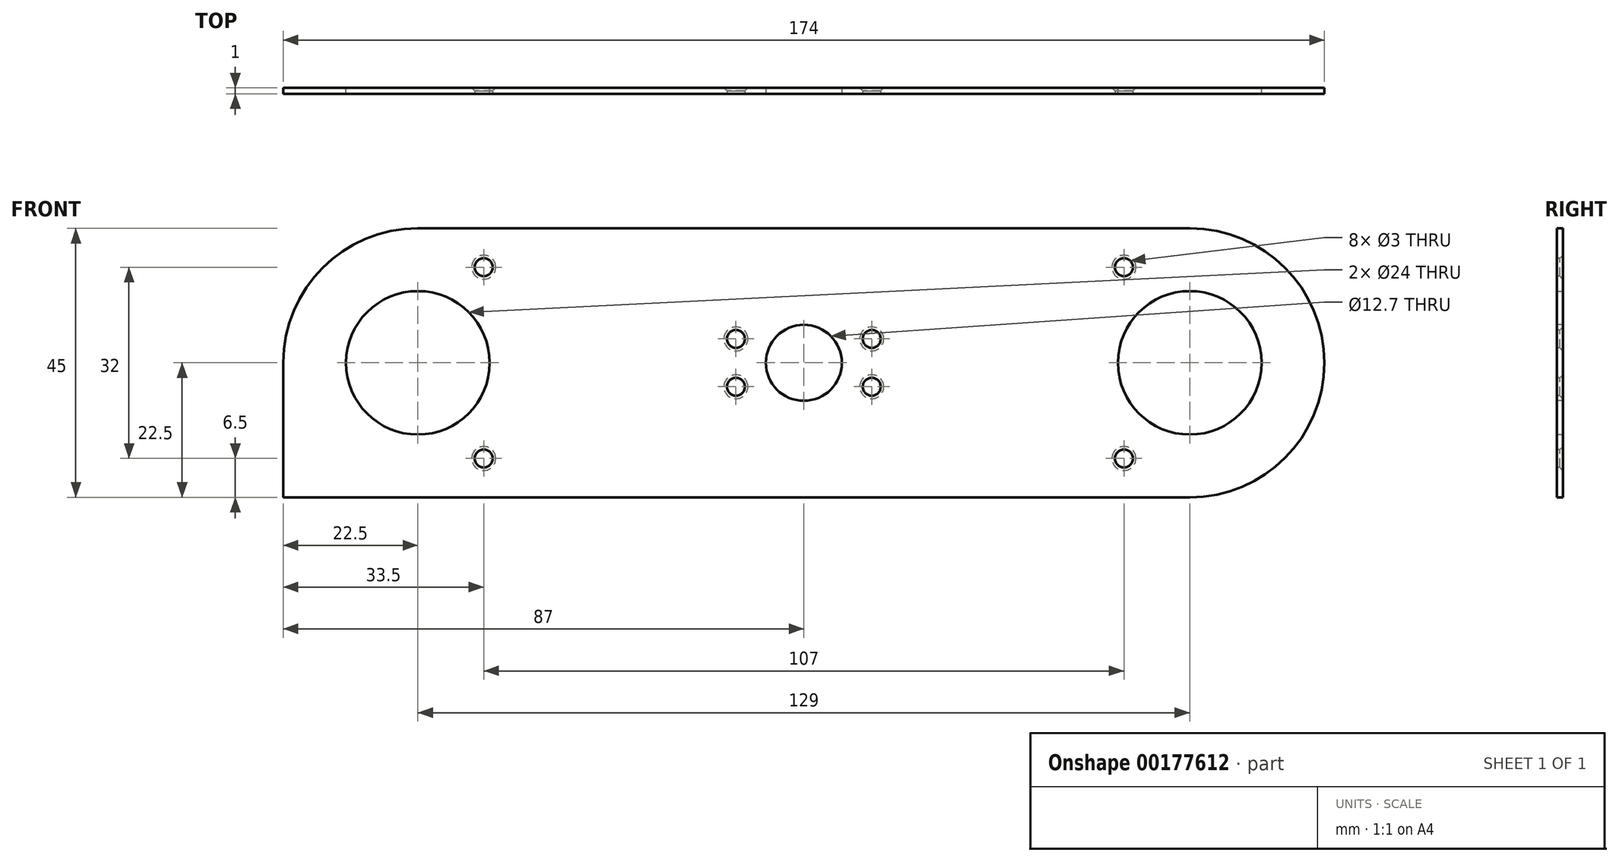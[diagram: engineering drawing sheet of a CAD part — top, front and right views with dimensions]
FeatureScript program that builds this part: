
annotation { "Feature Type Name" : "Feature", "Feature Type Description" : "" }
export const myFeature = defineFeature(function(context is Context, id is Id, definition is map)
    precondition{}
    {
        {
            var Q0;
            Q0=qCreatedBy(makeId("Front.planeOp"),FACE);
            var sketch = newSketch(context, id + "F0", { "sketchPlane" : qUnion([Q0])});
            skLineSegment(sketch, "E0.bottom", {"start": v(64.5, 22.5) * mm, "end": v(-64.5, 22.5) * mm});
            skLineSegment(sketch, "E0.top", {"start": v(64.5, -22.5) * mm, "end": v(-64.5, -22.5) * mm});
            skPoint(sketch, "E0.middle", {"position": v(0, 0) * mm});
            skCircle(sketch, "E1", {"center": v(64.5, 0) * mm, "radius": 12 * mm});
            skCircle(sketch, "E2", {"center": v(-64.5, 0) * mm, "radius": 12 * mm});
            skArc(sketch, "E3", {"start": v(-64.5, 22.5) * mm, "mid": v(-87, 0) * mm, "end": v(-64.5, -22.5) * mm});
            skArc(sketch, "E4", {"start": v(64.5, -22.5) * mm, "mid": v(87, 0) * mm, "end": v(64.5, 22.5) * mm});
            skPoint(sketch, "E5.orphan", {"position": v(-81.5, 22.5) * mm});
            skPoint(sketch, "E6.orphan", {"position": v(-81.5, -22.5) * mm});
            skPoint(sketch, "E7.orphan", {"position": v(81.5, 22.5) * mm});
            skPoint(sketch, "E8.orphan", {"position": v(81.5, -22.5) * mm});
            skSolve(sketch);
        }
        {
            var Q0;
            Q0 = qSketchRegion(id + "F0", true);
            extrude(context, id + "F1", {"entities" : qUnion([Q0]), "depth" : 1 * mm});
        }
        {
            var Q0;
            Q0=makeQuery(id+"F1.opExtrude","CAP_FACE",FACE,{"disambiguationData":[OSD([sQuery(id+"F0.wireOp",EDGE,"E0.bottom"),sQuery(id+"F0.wireOp",EDGE,"E0.top"),sQuery(id+"F0.wireOp",EDGE,"E1"),sQuery(id+"F0.wireOp",EDGE,"E2"),sQuery(id+"F0.wireOp",EDGE,"E3"),sQuery(id+"F0.wireOp",EDGE,"E4")])],"isStart":false});
            var sketch = newSketch(context, id + "F2", { "sketchPlane" : qUnion([Q0])});
            skLineSegment(sketch, "E9.top", {"start": v(-64.5, -22.5) * mm, "end": v(-87, -22.5) * mm});
            skLineSegment(sketch, "E9.right", {"start": v(-87, 0) * mm, "end": v(-87, -22.5) * mm});
            skPoint(sketch, "E9.left.start.orphan", {"position": v(-64.5, 0) * mm});
            skLineSegment(sketch, "E10", {"start": v(-87, 0) * mm, "end": v(-80.88, 0) * mm});
            skLineSegment(sketch, "E11", {"start": v(-80.88, 0) * mm, "end": v(-78.27, -9.46) * mm});
            skLineSegment(sketch, "E12", {"start": v(-78.27, -9.46) * mm, "end": v(-70.55, -14.76) * mm});
            skLineSegment(sketch, "E13", {"start": v(-70.55, -14.76) * mm, "end": v(-64.5, -17.43) * mm});
            skLineSegment(sketch, "E14", {"start": v(-64.5, -17.43) * mm, "end": v(-64.5, -22.5) * mm});
            skSolve(sketch);
        }
        {
            var Q0;
            Q0 = qSketchRegion(id + "F2", true);
            extrude(context, id + "F3", {"entities" : qUnion([Q0]), "operationType" : NewBodyOperationType.ADD, "oppositeDirection" : true, "depth" : 1 * mm});
        }
        {
            var Q0;
            Q0=makeQuery(id+"F3.boolean.opBoolean","MERGE",FACE,{"derivedFrom":[makeQuery(id+"F1.opExtrude","CAP_FACE",FACE,{"disambiguationData":[OSD([sQuery(id+"F0.wireOp",EDGE,"E0.bottom"),sQuery(id+"F0.wireOp",EDGE,"E0.top"),sQuery(id+"F0.wireOp",EDGE,"E1"),sQuery(id+"F0.wireOp",EDGE,"E2"),sQuery(id+"F0.wireOp",EDGE,"E3"),sQuery(id+"F0.wireOp",EDGE,"E4")])],"isStart":false}),makeQuery(id+"F3.opExtrude","CAP_FACE",FACE,{"disambiguationData":[OSD([sQuery(id+"F2.wireOp",EDGE,"E9.top"),sQuery(id+"F2.wireOp",EDGE,"E9.right"),sQuery(id+"F2.wireOp",EDGE,"E10"),sQuery(id+"F2.wireOp",EDGE,"E11"),sQuery(id+"F2.wireOp",EDGE,"E12"),sQuery(id+"F2.wireOp",EDGE,"E13"),sQuery(id+"F2.wireOp",EDGE,"E14")])],"isStart":true})]});
            var sketch = newSketch(context, id + "F4", { "sketchPlane" : qUnion([Q0])});
            skLineSegment(sketch, "E15.bottom", {"start": v(47, 22.5) * mm, "end": v(-47, 22.5) * mm, "construction": true});
            skLineSegment(sketch, "E15.top", {"start": v(47, -22.5) * mm, "end": v(-47, -22.5) * mm, "construction": true});
            skLineSegment(sketch, "E15.left", {"start": v(47, 22.5) * mm, "end": v(47, -22.5) * mm, "construction": true});
            skLineSegment(sketch, "E15.right", {"start": v(-47, 22.5) * mm, "end": v(-47, -22.5) * mm, "construction": true});
            skPoint(sketch, "E15.middle", {"position": v(0, 0) * mm});
            skLineSegment(sketch, "E16", {"start": v(-52.5, 0) * mm, "end": v(52.5, 0) * mm, "construction": true});
            skCircle(sketch, "E17", {"center": v(-53.5, 16) * mm, "radius": 1.5 * mm});
            skCircle(sketch, "E18", {"center": v(-53.5, -16) * mm, "radius": 1.5 * mm});
            skCircle(sketch, "E19", {"center": v(53.5, 16) * mm, "radius": 1.5 * mm});
            skCircle(sketch, "E20", {"center": v(53.5, -16) * mm, "radius": 1.5 * mm});
            skSolve(sketch);
        }
        {
            var Q0;
            Q0 = qSketchRegion(id + "F4", true);
            extrude(context, id + "F5", {"entities" : qUnion([Q0]), "operationType" : NewBodyOperationType.REMOVE, "oppositeDirection" : true, "depth" : 25 * mm});
        }
        {
            var Q0;
            Q0=makeQuery(id+"F5.boolean.opBoolean","INTERSECT",EDGE,{"derivedFrom":[makeQuery(id+"F3.boolean.opBoolean","MERGE",FACE,{"derivedFrom":[makeQuery(id+"F1.opExtrude","CAP_FACE",FACE,{"disambiguationData":[OSD([sQuery(id+"F0.wireOp",EDGE,"E0.bottom"),sQuery(id+"F0.wireOp",EDGE,"E0.top"),sQuery(id+"F0.wireOp",EDGE,"E1"),sQuery(id+"F0.wireOp",EDGE,"E2"),sQuery(id+"F0.wireOp",EDGE,"E3"),sQuery(id+"F0.wireOp",EDGE,"E4")])],"isStart":true}),makeQuery(id+"F3.opExtrude","CAP_FACE",FACE,{"disambiguationData":[OSD([sQuery(id+"F2.wireOp",EDGE,"E9.top"),sQuery(id+"F2.wireOp",EDGE,"E9.right"),sQuery(id+"F2.wireOp",EDGE,"E10"),sQuery(id+"F2.wireOp",EDGE,"E11"),sQuery(id+"F2.wireOp",EDGE,"E12"),sQuery(id+"F2.wireOp",EDGE,"E13"),sQuery(id+"F2.wireOp",EDGE,"E14")])],"isStart":false})]}),makeQuery(id+"F5.opExtrude","SWEPT_FACE",FACE,{"disambiguationData":[OSD([sQuery(id+"F4.wireOp",EDGE,"E17")])]})]});
            var Q1;
            Q1=makeQuery(id+"F5.boolean.opBoolean","INTERSECT",EDGE,{"derivedFrom":[makeQuery(id+"F3.boolean.opBoolean","MERGE",FACE,{"derivedFrom":[makeQuery(id+"F1.opExtrude","CAP_FACE",FACE,{"disambiguationData":[OSD([sQuery(id+"F0.wireOp",EDGE,"E0.bottom"),sQuery(id+"F0.wireOp",EDGE,"E0.top"),sQuery(id+"F0.wireOp",EDGE,"E1"),sQuery(id+"F0.wireOp",EDGE,"E2"),sQuery(id+"F0.wireOp",EDGE,"E3"),sQuery(id+"F0.wireOp",EDGE,"E4")])],"isStart":true}),makeQuery(id+"F3.opExtrude","CAP_FACE",FACE,{"disambiguationData":[OSD([sQuery(id+"F2.wireOp",EDGE,"E9.top"),sQuery(id+"F2.wireOp",EDGE,"E9.right"),sQuery(id+"F2.wireOp",EDGE,"E10"),sQuery(id+"F2.wireOp",EDGE,"E11"),sQuery(id+"F2.wireOp",EDGE,"E12"),sQuery(id+"F2.wireOp",EDGE,"E13"),sQuery(id+"F2.wireOp",EDGE,"E14")])],"isStart":false})]}),makeQuery(id+"F5.opExtrude","SWEPT_FACE",FACE,{"disambiguationData":[OSD([sQuery(id+"F4.wireOp",EDGE,"E18")])]})]});
            var Q2;
            Q2=makeQuery(id+"F5.boolean.opBoolean","INTERSECT",EDGE,{"derivedFrom":[makeQuery(id+"F3.boolean.opBoolean","MERGE",FACE,{"derivedFrom":[makeQuery(id+"F1.opExtrude","CAP_FACE",FACE,{"disambiguationData":[OSD([sQuery(id+"F0.wireOp",EDGE,"E0.bottom"),sQuery(id+"F0.wireOp",EDGE,"E0.top"),sQuery(id+"F0.wireOp",EDGE,"E1"),sQuery(id+"F0.wireOp",EDGE,"E2"),sQuery(id+"F0.wireOp",EDGE,"E3"),sQuery(id+"F0.wireOp",EDGE,"E4")])],"isStart":true}),makeQuery(id+"F3.opExtrude","CAP_FACE",FACE,{"disambiguationData":[OSD([sQuery(id+"F2.wireOp",EDGE,"E9.top"),sQuery(id+"F2.wireOp",EDGE,"E9.right"),sQuery(id+"F2.wireOp",EDGE,"E10"),sQuery(id+"F2.wireOp",EDGE,"E11"),sQuery(id+"F2.wireOp",EDGE,"E12"),sQuery(id+"F2.wireOp",EDGE,"E13"),sQuery(id+"F2.wireOp",EDGE,"E14")])],"isStart":false})]}),makeQuery(id+"F5.opExtrude","SWEPT_FACE",FACE,{"disambiguationData":[OSD([sQuery(id+"F4.wireOp",EDGE,"E19")])]})]});
            var Q3;
            Q3=makeQuery(id+"F5.boolean.opBoolean","INTERSECT",EDGE,{"derivedFrom":[makeQuery(id+"F3.boolean.opBoolean","MERGE",FACE,{"derivedFrom":[makeQuery(id+"F1.opExtrude","CAP_FACE",FACE,{"disambiguationData":[OSD([sQuery(id+"F0.wireOp",EDGE,"E0.bottom"),sQuery(id+"F0.wireOp",EDGE,"E0.top"),sQuery(id+"F0.wireOp",EDGE,"E1"),sQuery(id+"F0.wireOp",EDGE,"E2"),sQuery(id+"F0.wireOp",EDGE,"E3"),sQuery(id+"F0.wireOp",EDGE,"E4")])],"isStart":true}),makeQuery(id+"F3.opExtrude","CAP_FACE",FACE,{"disambiguationData":[OSD([sQuery(id+"F2.wireOp",EDGE,"E9.top"),sQuery(id+"F2.wireOp",EDGE,"E9.right"),sQuery(id+"F2.wireOp",EDGE,"E10"),sQuery(id+"F2.wireOp",EDGE,"E11"),sQuery(id+"F2.wireOp",EDGE,"E12"),sQuery(id+"F2.wireOp",EDGE,"E13"),sQuery(id+"F2.wireOp",EDGE,"E14")])],"isStart":false})]}),makeQuery(id+"F5.opExtrude","SWEPT_FACE",FACE,{"disambiguationData":[OSD([sQuery(id+"F4.wireOp",EDGE,"E20")])]})]});
            chamfer(context, id + "F6", {"entities" : qUnion([Q0, Q1, Q2, Q3]), "width" : .5 * mm, "tangentPropagation" : true});
        }
        {
            var Q0;
            Q0=makeQuery(id+"F3.boolean.opBoolean","MERGE",FACE,{"derivedFrom":[makeQuery(id+"F1.opExtrude","CAP_FACE",FACE,{"disambiguationData":[OSD([sQuery(id+"F0.wireOp",EDGE,"E0.bottom"),sQuery(id+"F0.wireOp",EDGE,"E0.top"),sQuery(id+"F0.wireOp",EDGE,"E1"),sQuery(id+"F0.wireOp",EDGE,"E2"),sQuery(id+"F0.wireOp",EDGE,"E3"),sQuery(id+"F0.wireOp",EDGE,"E4")])],"isStart":false}),makeQuery(id+"F3.opExtrude","CAP_FACE",FACE,{"disambiguationData":[OSD([sQuery(id+"F2.wireOp",EDGE,"E9.top"),sQuery(id+"F2.wireOp",EDGE,"E9.right"),sQuery(id+"F2.wireOp",EDGE,"E10"),sQuery(id+"F2.wireOp",EDGE,"E11"),sQuery(id+"F2.wireOp",EDGE,"E12"),sQuery(id+"F2.wireOp",EDGE,"E13"),sQuery(id+"F2.wireOp",EDGE,"E14")])],"isStart":true})]});
            var sketch = newSketch(context, id + "F7", { "sketchPlane" : qUnion([Q0])});
            skCircle(sketch, "E21", {"center": v(0, 0) * mm, "radius": 6.35 * mm});
            skSolve(sketch);
        }
        {
            var Q0;
            Q0 = qSketchRegion(id + "F7", true);
            extrude(context, id + "F8", {"entities" : qUnion([Q0]), "operationType" : NewBodyOperationType.REMOVE, "oppositeDirection" : true, "depth" : 25 * mm});
        }
        {
            var Q0;
            Q0=makeQuery(id+"F3.boolean.opBoolean","MERGE",FACE,{"derivedFrom":[makeQuery(id+"F1.opExtrude","CAP_FACE",FACE,{"disambiguationData":[OSD([sQuery(id+"F0.wireOp",EDGE,"E0.bottom"),sQuery(id+"F0.wireOp",EDGE,"E0.top"),sQuery(id+"F0.wireOp",EDGE,"E1"),sQuery(id+"F0.wireOp",EDGE,"E2"),sQuery(id+"F0.wireOp",EDGE,"E3"),sQuery(id+"F0.wireOp",EDGE,"E4")])],"isStart":false}),makeQuery(id+"F3.opExtrude","CAP_FACE",FACE,{"disambiguationData":[OSD([sQuery(id+"F2.wireOp",EDGE,"E9.top"),sQuery(id+"F2.wireOp",EDGE,"E9.right"),sQuery(id+"F2.wireOp",EDGE,"E10"),sQuery(id+"F2.wireOp",EDGE,"E11"),sQuery(id+"F2.wireOp",EDGE,"E12"),sQuery(id+"F2.wireOp",EDGE,"E13"),sQuery(id+"F2.wireOp",EDGE,"E14")])],"isStart":true})]});
            var sketch = newSketch(context, id + "F9", { "sketchPlane" : qUnion([Q0])});
            skPoint(sketch, "E22.middle", {"position": v(0, 0) * mm});
            skCircle(sketch, "E23", {"center": v(-11.35, 4) * mm, "radius": 1.5 * mm});
            skCircle(sketch, "E24", {"center": v(-11.35, -4) * mm, "radius": 1.5 * mm});
            skCircle(sketch, "E25", {"center": v(11.35, 4) * mm, "radius": 1.5 * mm});
            skCircle(sketch, "E26", {"center": v(11.35, -4) * mm, "radius": 1.5 * mm});
            skPoint(sketch, "E27.orphan", {"position": v(-11.35, 11.35) * mm});
            skPoint(sketch, "E28.orphan", {"position": v(11.35, 11.35) * mm});
            skPoint(sketch, "E22.top.start.orphan", {"position": v(11.35, -11.35) * mm});
            skPoint(sketch, "E29.orphan", {"position": v(-11.35, -11.35) * mm});
            skLineSegment(sketch, "E30", {"start": v(52.5, 0) * mm, "end": v(-52.5, 0) * mm, "construction": true});
            skLineSegment(sketch, "E31", {"start": v(-52.5, 0) * mm, "end": v(0, 0) * mm, "construction": true});
            skLineSegment(sketch, "E32", {"start": v(0, 22.5) * mm, "end": v(0, -22.5) * mm, "construction": true});
            skLineSegment(sketch, "E33.bottom", {"start": v(11.35, 11.35) * mm, "end": v(-11.35, 11.35) * mm, "construction": true});
            skLineSegment(sketch, "E33.top", {"start": v(11.35, -11.35) * mm, "end": v(-11.35, -11.35) * mm, "construction": true});
            skLineSegment(sketch, "E33.left", {"start": v(11.35, 11.35) * mm, "end": v(11.35, -11.35) * mm, "construction": true});
            skLineSegment(sketch, "E33.right", {"start": v(-11.35, 11.35) * mm, "end": v(-11.35, -11.35) * mm, "construction": true});
            skSolve(sketch);
        }
        {
            var Q0;
            Q0 = qSketchRegion(id + "F9", true);
            extrude(context, id + "F10", {"entities" : qUnion([Q0]), "operationType" : NewBodyOperationType.REMOVE, "oppositeDirection" : true, "depth" : 25 * mm});
        }
        {
            var Q0;
            Q0=makeQuery(id+"F10.boolean.opBoolean","INTERSECT",EDGE,{"derivedFrom":[makeQuery(id+"F3.boolean.opBoolean","MERGE",FACE,{"derivedFrom":[makeQuery(id+"F1.opExtrude","CAP_FACE",FACE,{"disambiguationData":[OSD([sQuery(id+"F0.wireOp",EDGE,"E0.bottom"),sQuery(id+"F0.wireOp",EDGE,"E0.top"),sQuery(id+"F0.wireOp",EDGE,"E1"),sQuery(id+"F0.wireOp",EDGE,"E2"),sQuery(id+"F0.wireOp",EDGE,"E3"),sQuery(id+"F0.wireOp",EDGE,"E4")])],"isStart":true}),makeQuery(id+"F3.opExtrude","CAP_FACE",FACE,{"disambiguationData":[OSD([sQuery(id+"F2.wireOp",EDGE,"E9.top"),sQuery(id+"F2.wireOp",EDGE,"E9.right"),sQuery(id+"F2.wireOp",EDGE,"E10"),sQuery(id+"F2.wireOp",EDGE,"E11"),sQuery(id+"F2.wireOp",EDGE,"E12"),sQuery(id+"F2.wireOp",EDGE,"E13"),sQuery(id+"F2.wireOp",EDGE,"E14")])],"isStart":false})]}),makeQuery(id+"F10.opExtrude","SWEPT_FACE",FACE,{"disambiguationData":[OSD([sQuery(id+"F9.wireOp",EDGE,"E23")])]})]});
            var Q1;
            Q1=makeQuery(id+"F10.boolean.opBoolean","INTERSECT",EDGE,{"derivedFrom":[makeQuery(id+"F3.boolean.opBoolean","MERGE",FACE,{"derivedFrom":[makeQuery(id+"F1.opExtrude","CAP_FACE",FACE,{"disambiguationData":[OSD([sQuery(id+"F0.wireOp",EDGE,"E0.bottom"),sQuery(id+"F0.wireOp",EDGE,"E0.top"),sQuery(id+"F0.wireOp",EDGE,"E1"),sQuery(id+"F0.wireOp",EDGE,"E2"),sQuery(id+"F0.wireOp",EDGE,"E3"),sQuery(id+"F0.wireOp",EDGE,"E4")])],"isStart":true}),makeQuery(id+"F3.opExtrude","CAP_FACE",FACE,{"disambiguationData":[OSD([sQuery(id+"F2.wireOp",EDGE,"E9.top"),sQuery(id+"F2.wireOp",EDGE,"E9.right"),sQuery(id+"F2.wireOp",EDGE,"E10"),sQuery(id+"F2.wireOp",EDGE,"E11"),sQuery(id+"F2.wireOp",EDGE,"E12"),sQuery(id+"F2.wireOp",EDGE,"E13"),sQuery(id+"F2.wireOp",EDGE,"E14")])],"isStart":false})]}),makeQuery(id+"F10.opExtrude","SWEPT_FACE",FACE,{"disambiguationData":[OSD([sQuery(id+"F9.wireOp",EDGE,"E24")])]})]});
            var Q2;
            Q2=makeQuery(id+"F10.boolean.opBoolean","INTERSECT",EDGE,{"derivedFrom":[makeQuery(id+"F3.boolean.opBoolean","MERGE",FACE,{"derivedFrom":[makeQuery(id+"F1.opExtrude","CAP_FACE",FACE,{"disambiguationData":[OSD([sQuery(id+"F0.wireOp",EDGE,"E0.bottom"),sQuery(id+"F0.wireOp",EDGE,"E0.top"),sQuery(id+"F0.wireOp",EDGE,"E1"),sQuery(id+"F0.wireOp",EDGE,"E2"),sQuery(id+"F0.wireOp",EDGE,"E3"),sQuery(id+"F0.wireOp",EDGE,"E4")])],"isStart":true}),makeQuery(id+"F3.opExtrude","CAP_FACE",FACE,{"disambiguationData":[OSD([sQuery(id+"F2.wireOp",EDGE,"E9.top"),sQuery(id+"F2.wireOp",EDGE,"E9.right"),sQuery(id+"F2.wireOp",EDGE,"E10"),sQuery(id+"F2.wireOp",EDGE,"E11"),sQuery(id+"F2.wireOp",EDGE,"E12"),sQuery(id+"F2.wireOp",EDGE,"E13"),sQuery(id+"F2.wireOp",EDGE,"E14")])],"isStart":false})]}),makeQuery(id+"F10.opExtrude","SWEPT_FACE",FACE,{"disambiguationData":[OSD([sQuery(id+"F9.wireOp",EDGE,"E26")])]})]});
            var Q3;
            Q3=makeQuery(id+"F10.boolean.opBoolean","INTERSECT",EDGE,{"derivedFrom":[makeQuery(id+"F3.boolean.opBoolean","MERGE",FACE,{"derivedFrom":[makeQuery(id+"F1.opExtrude","CAP_FACE",FACE,{"disambiguationData":[OSD([sQuery(id+"F0.wireOp",EDGE,"E0.bottom"),sQuery(id+"F0.wireOp",EDGE,"E0.top"),sQuery(id+"F0.wireOp",EDGE,"E1"),sQuery(id+"F0.wireOp",EDGE,"E2"),sQuery(id+"F0.wireOp",EDGE,"E3"),sQuery(id+"F0.wireOp",EDGE,"E4")])],"isStart":true}),makeQuery(id+"F3.opExtrude","CAP_FACE",FACE,{"disambiguationData":[OSD([sQuery(id+"F2.wireOp",EDGE,"E9.top"),sQuery(id+"F2.wireOp",EDGE,"E9.right"),sQuery(id+"F2.wireOp",EDGE,"E10"),sQuery(id+"F2.wireOp",EDGE,"E11"),sQuery(id+"F2.wireOp",EDGE,"E12"),sQuery(id+"F2.wireOp",EDGE,"E13"),sQuery(id+"F2.wireOp",EDGE,"E14")])],"isStart":false})]}),makeQuery(id+"F10.opExtrude","SWEPT_FACE",FACE,{"disambiguationData":[OSD([sQuery(id+"F9.wireOp",EDGE,"E25")])]})]});
            chamfer(context, id + "F11", {"entities" : qUnion([Q0, Q1, Q2, Q3]), "width" : .5 * mm, "tangentPropagation" : true});
        }
    });
